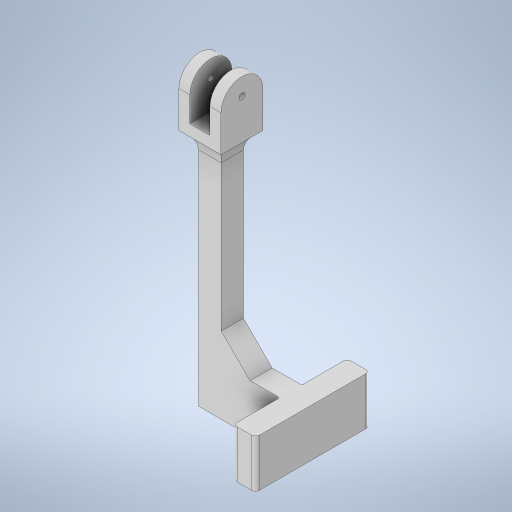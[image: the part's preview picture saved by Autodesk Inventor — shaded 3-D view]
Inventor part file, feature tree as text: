
AUTODESK INVENTOR PART (.ipt)
format: ipt  version: 2023 (Build 270158000, 158)  size: 326,656 bytes
history: native  units: mm
features: extrude x6, sketch x6, fillet x4, other x1, chamfer x1
ambient origin geometry x8: Origin, YZ Plane, XZ Plane, XY Plane, X Axis, Y Axis, Z Axis, Center Point
bodies: Body1 (feature_tree)
feature tree (18):
  other  "實體1"
  extrude  "擠出1"  Depth=12.0mm
  extrude  "擠出2"  Depth=11.6mm
  extrude  "擠出3"  Depth=125.0mm TaperAngle=0.0deg
  extrude  "擠出4"  Depth=25.0mm
  extrude  "擠出5"  Depth=30.5mm TaperAngle=0.0deg
  extrude  "擠出6"  Depth=25.0mm
  fillet  "圓角1"  Radius=59.6mm
  fillet  "圓角2"  Radius=23.8mm
  chamfer  "倒角1"  Distance=11.6mm
  fillet  "圓角3"  Radius=22.0mm
  fillet  "圓角4"  Radius=22.0mm
  sketch  "草圖1"
  sketch  "草圖2"
  sketch  "草圖3"
  sketch  "草圖4"
  sketch  "草圖5"
  sketch  "草圖6"
